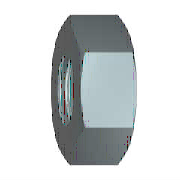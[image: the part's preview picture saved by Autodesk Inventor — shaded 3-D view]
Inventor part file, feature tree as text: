
AUTODESK INVENTOR PART (.ipt)
format: ipt  version: 2020 (Build 240168000, 168)  size: 164,352 bytes
history: native  units: mm (DEFAULTED — no unit token found)
features: sketch x3, chamfer x1, hole x1, other x1, plane x1
ambient origin geometry x7: Origin, YZ Plane, XZ Plane, X Axis, Y Axis, Z Axis, Center Point
bodies: Solid1 (feature_tree), Body (feature_tree)
feature tree (7):
  chamfer  "Chamfer1"  Angle=30.0deg  [1 undecoded]
  hole  "Thread"  [1 undecoded]
  other  "Work Axis1"
  plane  "Work Plane1"
  sketch  "Sketch1"  dims[d0=6.350853mm]
  sketch  "Sketch2"  dims[d1=2.4mm]
  sketch  "Sketch3"  dims[d2=0.0mm d3=30.0deg d4=30.0deg d5=4.6mm d6=4.6mm d7=90.0deg d25=2.459mm d26=6.0mm d27=4.0mm d28=2.0mm d29=14.3117mm d30=8.0mm d31=20.594885mm d8=0.270633mm d9=30.0deg d10=0.270633mm d11=30.0deg d13=0.0mm d14=0.0mm d39=0.0mm d40=0.270633mm d41=0.270633mm d42=0.0mm]
note: 2 required parameter values undecoded (feature->parameter linkage not recoverable at this tier; creation-order binding heuristic only, values carry confidence <= 0.55)
